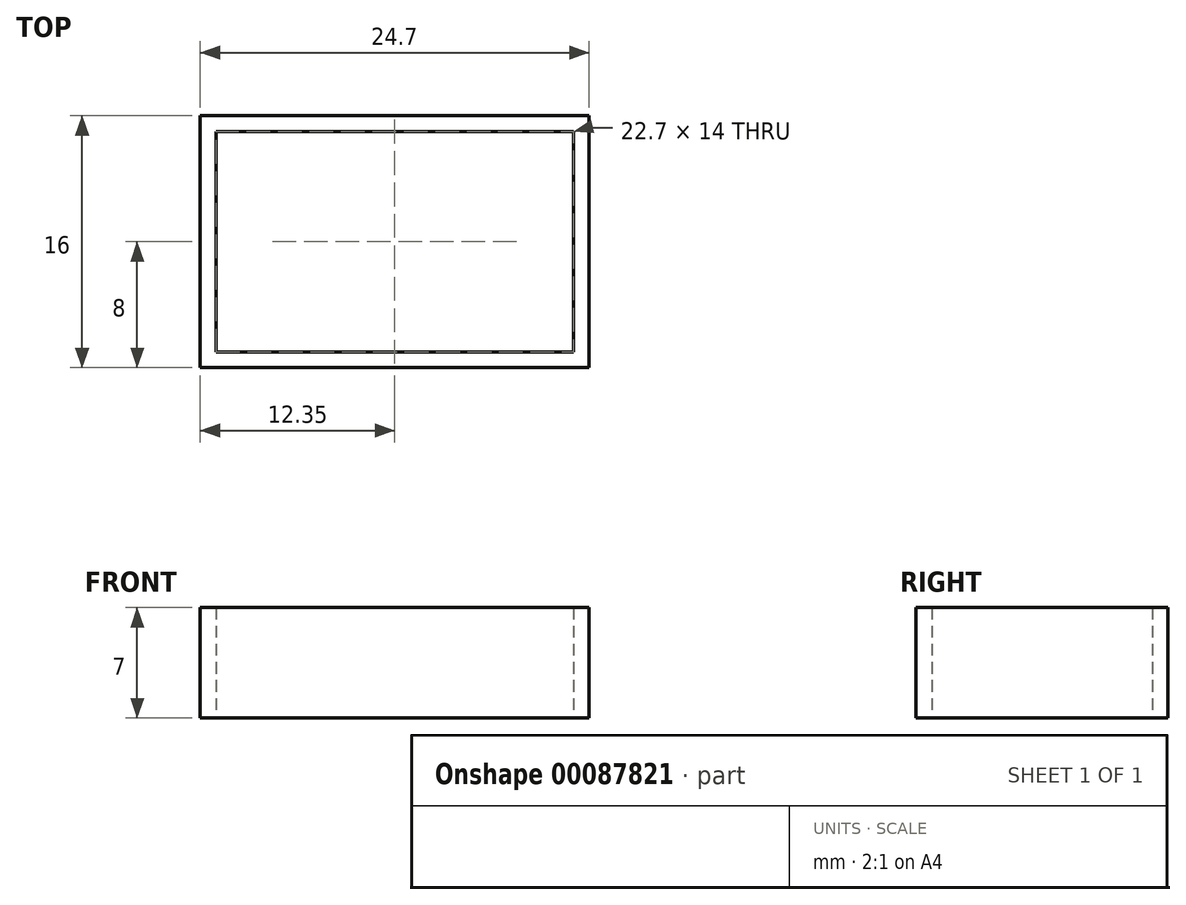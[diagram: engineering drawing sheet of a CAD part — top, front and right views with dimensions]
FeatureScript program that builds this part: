
annotation { "Feature Type Name" : "Feature", "Feature Type Description" : "" }
export const myFeature = defineFeature(function(context is Context, id is Id, definition is map)
    precondition{}
    {
        {
            var Q0;
            Q0=qCreatedBy(makeId("Top.planeOp"),FACE);
            var sketch = newSketch(context, id + "F0", { "sketchPlane" : qUnion([Q0])});
            skLineSegment(sketch, "E0.bottom", {"start": v(0, 0) * mm, "end": v(22.7, 0) * mm});
            skLineSegment(sketch, "E0.top", {"start": v(0, 14) * mm, "end": v(22.7, 14) * mm});
            skLineSegment(sketch, "E0.left", {"start": v(0, 0) * mm, "end": v(0, 4.5) * mm});
            skLineSegment(sketch, "E0.right", {"start": v(22.7, 0) * mm, "end": v(22.7, 4.5) * mm});
            skLineSegment(sketch, "E1.left", {"start": v(0, 4.5) * mm, "end": v(0, 9.5) * mm});
            skLineSegment(sketch, "E2.left", {"start": v(22.7, 4.5) * mm, "end": v(22.7, 9.5) * mm});
            skLineSegment(sketch, "E3", {"start": v(22.7, 9.5) * mm, "end": v(22.7, 14) * mm});
            skLineSegment(sketch, "E4", {"start": v(0, 9.5) * mm, "end": v(0, 14) * mm});
            skLineSegment(sketch, "E5.0", {"start": v(-1, 9.5) * mm, "end": v(-1, 15) * mm});
            skLineSegment(sketch, "E5.1", {"start": v(-1, 4.5) * mm, "end": v(-1, 9.5) * mm});
            skLineSegment(sketch, "E5.2", {"start": v(-1, 15) * mm, "end": v(23.7, 15) * mm});
            skLineSegment(sketch, "E5.3", {"start": v(-1, -1) * mm, "end": v(-1, 4.5) * mm});
            skLineSegment(sketch, "E5.4", {"start": v(23.7, 9.5) * mm, "end": v(23.7, 15) * mm});
            skLineSegment(sketch, "E5.5", {"start": v(23.7, 4.5) * mm, "end": v(23.7, 9.5) * mm});
            skLineSegment(sketch, "E5.6", {"start": v(23.7, -1) * mm, "end": v(23.7, 4.5) * mm});
            skLineSegment(sketch, "E5.7", {"start": v(-1, -1) * mm, "end": v(23.7, -1) * mm});
            skSolve(sketch);
        }
        {
            var Q0;
            Q0=makeQuery(id+"F0.imprint","IMPRINT",FACE,{"disambiguationData":[TD([[makeQuery(id+"F0.imprint","IMPRINT",EDGE,{"derivedFrom":sQuery(id+"F0.wireOp",EDGE,"E0.bottom")}),-1.0]])]});
            extrude(context, id + "F1", {"entities" : qUnion([Q0]), "depth" : 7 * mm});
        }
    });
